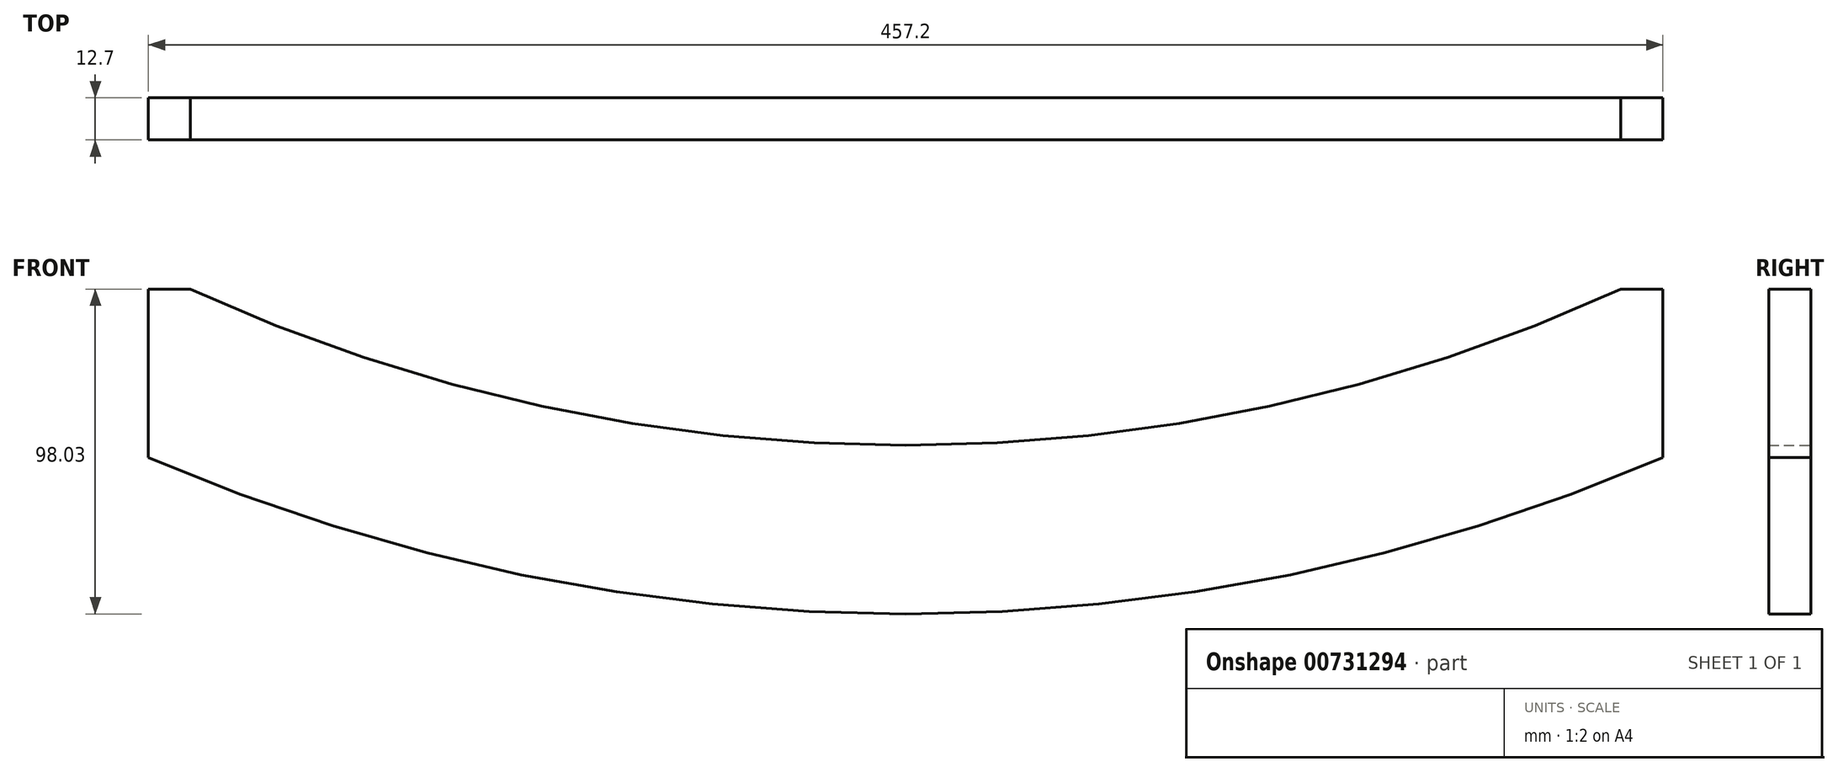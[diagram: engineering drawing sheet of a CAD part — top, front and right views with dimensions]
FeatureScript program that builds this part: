
annotation { "Feature Type Name" : "Feature", "Feature Type Description" : "" }
export const myFeature = defineFeature(function(context is Context, id is Id, definition is map)
    precondition{}
    {
        {
            var Q0;
            Q0=qCreatedBy(makeId("Front.planeOp"),FACE);
            var sketch = newSketch(context, id + "F0", { "sketchPlane" : qUnion([Q0])});
            skLineSegment(sketch, "E0", {"start": v(0, 98.03) * mm, "end": v(12.7, 98.03) * mm});
            skLineSegment(sketch, "E1", {"start": v(0, 98.03) * mm, "end": v(0, 47.23) * mm});
            skPoint(sketch, "E2", {"position": v(228.6, 0) * mm});
            skLineSegment(sketch, "E3", {"start": v(444.5, 98.03) * mm, "end": v(457.2, 98.03) * mm});
            skLineSegment(sketch, "E4", {"start": v(457.2, 98.03) * mm, "end": v(457.2, 47.23) * mm});
            skArc(sketch, "E5", {"start": v(0, 47.23) * mm, "mid": v(228.6, 0) * mm, "end": v(457.2, 47.23) * mm});
            skArc(sketch, "E6", {"start": v(12.7, 98.03) * mm, "mid": v(228.6, 50.87) * mm, "end": v(444.5, 98.03) * mm});
            skPoint(sketch, "E7.start.orphan", {"position": v(228.6, 98.03) * mm});
            skPoint(sketch, "E8.orphan", {"position": v(0, 0) * mm});
            skPoint(sketch, "E9.end.orphan", {"position": v(457.2, 0) * mm});
            skPoint(sketch, "E10", {"position": v(228.6, 50.87) * mm});
            skSolve(sketch);
        }
        {
            var Q0;
            Q0=makeQuery(id+"F0.imprint","IMPRINT",FACE,{"disambiguationData":[TD([[makeQuery(id+"F0.imprint","IMPRINT",EDGE,{"derivedFrom":sQuery(id+"F0.wireOp",EDGE,"E0")}),-1.0]])]});
            extrude(context, id + "F1", {"entities" : qUnion([Q0]), "depth" : 12.7 * mm, "offsetDistance" : 25.4 * mm});
        }
    });
